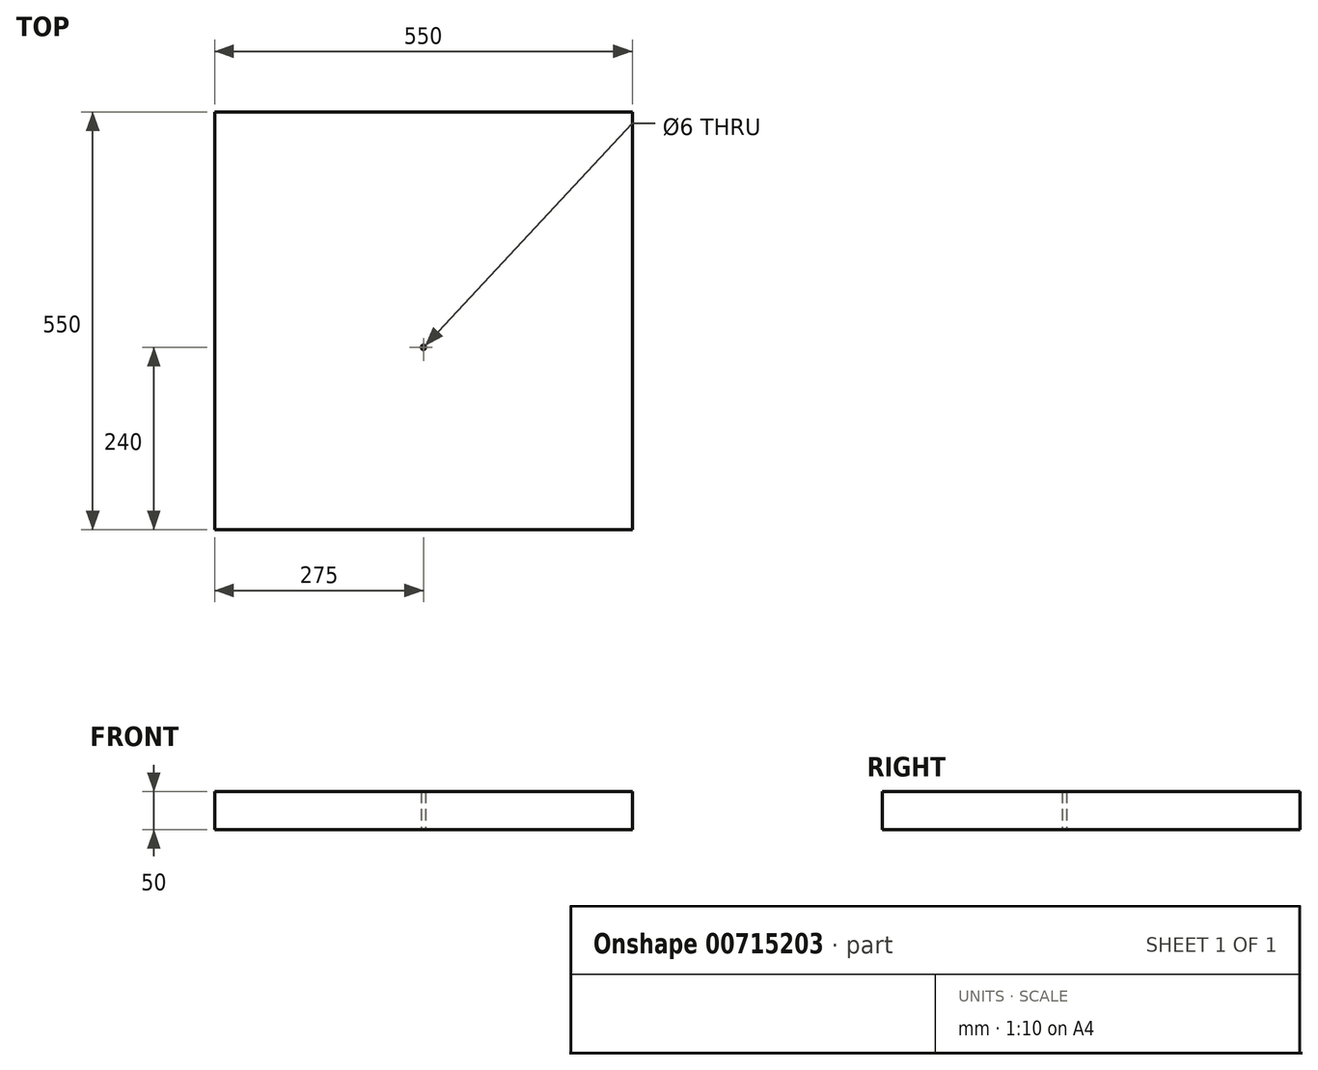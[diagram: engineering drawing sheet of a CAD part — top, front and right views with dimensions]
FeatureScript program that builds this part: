
annotation { "Feature Type Name" : "Feature", "Feature Type Description" : "" }
export const myFeature = defineFeature(function(context is Context, id is Id, definition is map)
    precondition{}
    {
        {
            var Q0;
            Q0=qCreatedBy(makeId("Top.planeOp"),FACE);
            var sketch = newSketch(context, id + "F0", { "sketchPlane" : qUnion([Q0])});
            skLineSegment(sketch, "E0.bottom", {"start": v(275, 275) * mm, "end": v(-275, 275) * mm});
            skLineSegment(sketch, "E0.top", {"start": v(275, -275) * mm, "end": v(-275, -275) * mm});
            skLineSegment(sketch, "E0.left", {"start": v(275, 275) * mm, "end": v(275, -275) * mm});
            skLineSegment(sketch, "E0.right", {"start": v(-275, 275) * mm, "end": v(-275, -275) * mm});
            skPoint(sketch, "E0.middle", {"position": v(0, 0) * mm});
            skLineSegment(sketch, "E1.0", {"start": v(272.5, 272.5) * mm, "end": v(-272.5, 272.5) * mm});
            skLineSegment(sketch, "E1.1", {"start": v(272.5, 272.5) * mm, "end": v(272.5, -272.5) * mm});
            skLineSegment(sketch, "E1.2", {"start": v(272.5, -272.5) * mm, "end": v(-272.5, -272.5) * mm});
            skLineSegment(sketch, "E1.3", {"start": v(-272.5, 272.5) * mm, "end": v(-272.5, -272.5) * mm});
            skLineSegment(sketch, "E2.bottom", {"start": v(-272.5, 272.5) * mm, "end": v(-222.5, 272.5) * mm});
            skLineSegment(sketch, "E2.top", {"start": v(-272.5, 222.5) * mm, "end": v(-222.5, 222.5) * mm});
            skLineSegment(sketch, "E2.left", {"start": v(-272.5, 272.5) * mm, "end": v(-272.5, 222.5) * mm});
            skLineSegment(sketch, "E2.right", {"start": v(-222.5, 272.5) * mm, "end": v(-222.5, 222.5) * mm});
            skLineSegment(sketch, "E3", {"start": v(0, 275) * mm, "end": v(0, -272.5) * mm, "construction": true});
            skLineSegment(sketch, "E4", {"start": v(-272.5, 0) * mm, "end": v(272.5, 0) * mm, "construction": true});
            skLineSegment(sketch, "E5.MirrorCS", {"start": v(272.5, 222.5) * mm, "end": v(222.5, 222.5) * mm});
            skLineSegment(sketch, "E6.MirrorCS", {"start": v(222.5, 272.5) * mm, "end": v(222.5, 222.5) * mm});
            skLineSegment(sketch, "E7.MirrorCS", {"start": v(-272.5, -222.5) * mm, "end": v(-222.5, -222.5) * mm});
            skLineSegment(sketch, "E8.MirrorCS", {"start": v(-222.5, -272.5) * mm, "end": v(-222.5, -222.5) * mm});
            skLineSegment(sketch, "E9.MirrorCS", {"start": v(222.5, -272.5) * mm, "end": v(222.5, -222.5) * mm});
            skLineSegment(sketch, "E10.MirrorCS", {"start": v(272.5, -222.5) * mm, "end": v(222.5, -222.5) * mm});
            skCircle(sketch, "E11", {"center": v(0, -35) * mm, "radius": 3 * mm});
            skSolve(sketch);
        }
        {
            var Q0;
            {var subQ3=sQuery(id+"F0.wireOp",EDGE,"E2.top");Q0=makeQuery(id+"F0.imprint","IMPRINT",FACE,{"disambiguationData":[TD([[makeQuery(id+"F0.imprint","IMPRINT",EDGE,{"derivedFrom":subQ3}),-1.0]])]});}
            var Q1;
            Q1=makeQuery(id+"F0.imprint","IMPRINT",FACE,{"disambiguationData":[TD([[makeQuery(id+"F0.imprint","IMPRINT",EDGE,{"derivedFrom":sQuery(id+"F0.wireOp",EDGE,"E0.bottom")}),1.0]])]});
            var Q2;
            {var subQ4=sQuery(id+"F0.wireOp",EDGE,"E2.top");Q2=makeQuery(id+"F0.imprint","IMPRINT",FACE,{"disambiguationData":[TD([[makeQuery(id+"F0.imprint","IMPRINT",EDGE,{"derivedFrom":subQ4}),1.0]])]});}
            var Q3;
            {var subQ4=sQuery(id+"F0.wireOp",EDGE,"E9.MirrorCS");Q3=makeQuery(id+"F0.imprint","IMPRINT",FACE,{"disambiguationData":[TD([[makeQuery(id+"F0.imprint","IMPRINT",EDGE,{"derivedFrom":subQ4}),-1.0]])]});}
            var Q4;
            {var subQ4=sQuery(id+"F0.wireOp",EDGE,"E5.MirrorCS");Q4=makeQuery(id+"F0.imprint","IMPRINT",FACE,{"disambiguationData":[TD([[makeQuery(id+"F0.imprint","IMPRINT",EDGE,{"derivedFrom":subQ4}),-1.0]])]});}
            var Q5;
            {var subQ4=sQuery(id+"F0.wireOp",EDGE,"E7.MirrorCS");Q5=makeQuery(id+"F0.imprint","IMPRINT",FACE,{"disambiguationData":[TD([[makeQuery(id+"F0.imprint","IMPRINT",EDGE,{"derivedFrom":subQ4}),-1.0]])]});}
            extrude(context, id + "F1", {"entities" : qUnion([Q0, Q1, Q2, Q3, Q4, Q5]), "depth" : 50 * mm, "offsetDistance" : 25 * mm});
        }
    });
